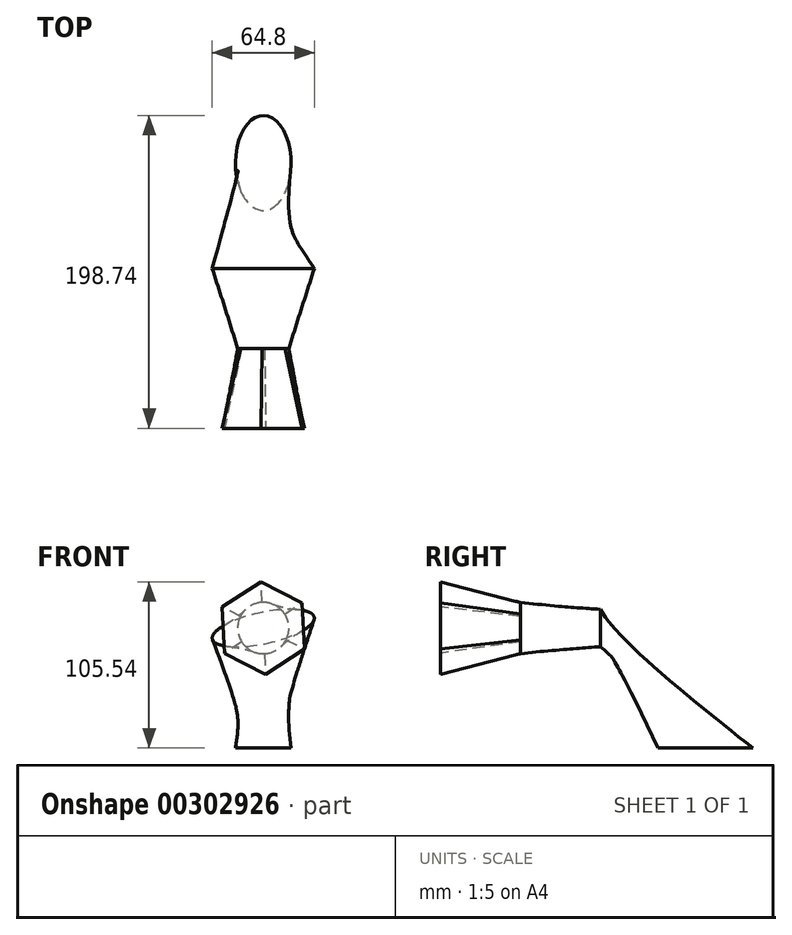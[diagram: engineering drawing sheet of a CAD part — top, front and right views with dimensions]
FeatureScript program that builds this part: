
annotation { "Feature Type Name" : "Feature", "Feature Type Description" : "" }
export const myFeature = defineFeature(function(context is Context, id is Id, definition is map)
    precondition{}
    {
        {
            var Q0;
            Q0=qCreatedBy(makeId("Front.planeOp"),FACE);
            var sketch = newSketch(context, id + "F0", { "sketchPlane" : qUnion([Q0])});
            skEllipse(sketch, "E0", {"center": v(0, 0) * mm, "majorRadius": 33.07 * mm, "minorRadius": 9.9 * mm, "majorAxis": v(0.98, 0.2)});
            skSolve(sketch);
        }
        {
            var Q0;
            Q0=qCreatedBy(makeId("Front.planeOp"),FACE);
            cPlane(context, id + "F1", {"entities" : qUnion([Q0]), "cplaneType" : CPlaneType.OFFSET, "offset" : 101.6 * mm, "width" : 152.4 * mm, "height" : 152.4 * mm});
        }
        {
            var Q0;
            Q0=qCreatedBy(makeId("Front.planeOp"),FACE);
            cPlane(context, id + "F2", {"entities" : qUnion([Q0]), "cplaneType" : CPlaneType.OFFSET, "offset" : 50.8 * mm, "width" : 152.4 * mm, "height" : 152.4 * mm});
        }
        {
            var Q0;
            Q0=qCreatedBy(id+"F2.planeOp",FACE);
            var sketch = newSketch(context, id + "F3", { "sketchPlane" : qUnion([Q0])});
            skCircle(sketch, "E1", {"center": v(0, 0) * mm, "radius": 16.28 * mm});
            skSolve(sketch);
        }
        {
            var Q0;
            Q0=qCreatedBy(id+"F1.planeOp",FACE);
            var sketch = newSketch(context, id + "F4", { "sketchPlane" : qUnion([Q0])});
            skCircle(sketch, "E2.cCircle", {"center": v(0, 0) * mm, "radius": 25.45 * mm, "construction": true});
            skLineSegment(sketch, "E2.0", {"start": v(26.17, -13.37) * mm, "end": v(1.5, -29.34) * mm});
            skLineSegment(sketch, "E2.1", {"start": v(1.5, -29.34) * mm, "end": v(-24.66, -15.98) * mm});
            skLineSegment(sketch, "E2.2", {"start": v(-24.66, -15.98) * mm, "end": v(-26.17, 13.37) * mm});
            skLineSegment(sketch, "E2.3", {"start": v(-26.17, 13.37) * mm, "end": v(-1.5, 29.34) * mm});
            skLineSegment(sketch, "E2.4", {"start": v(-1.5, 29.34) * mm, "end": v(24.66, 15.98) * mm});
            skLineSegment(sketch, "E2.5", {"start": v(24.66, 15.98) * mm, "end": v(26.17, -13.37) * mm});
            skPoint(sketch, "E2.0.midPoint", {"position": v(13.84, -21.36) * mm});
            skSolve(sketch);
        }
        {
            var Q0;
            Q0=makeQuery(id+"F0.imprint","IMPRINT",FACE,{"disambiguationData":[TD([[makeQuery(id+"F0.imprint","IMPRINT",EDGE,{"derivedFrom":sQuery(id+"F0.wireOp",EDGE,"E0")}),1.0]])]});
            var Q1;
            Q1=makeQuery(id+"F3.imprint","IMPRINT",FACE,{"disambiguationData":[TD([[makeQuery(id+"F3.imprint","IMPRINT",EDGE,{"derivedFrom":sQuery(id+"F3.wireOp",EDGE,"E1")}),1.0]])]});
            loft(context, id + "F5", {"sheetProfilesArray" : [{ "sheetProfileEntities" : qUnion([Q0]) }, { "sheetProfileEntities" : qUnion([Q1]) }]});
        }
        {
            var Q1;
            Q1=makeQuery(id+"F5.opLoft","CAP_FACE",FACE,{"disambiguationData":[OSD([makeQuery(id+"F3.imprint","IMPRINT",FACE,{"disambiguationData":[TD([[makeQuery(id+"F3.imprint","IMPRINT",EDGE,{"derivedFrom":sQuery(id+"F3.wireOp",EDGE,"E1")}),1.0]])]})])],"isStart":true});
            var Q2;
            Q2=makeQuery(id+"F4.imprint","IMPRINT",FACE,{"disambiguationData":[TD([[makeQuery(id+"F4.imprint","IMPRINT",EDGE,{"derivedFrom":sQuery(id+"F4.wireOp",EDGE,"E2.0")}),-1.0]])]});
            loft(context, id + "F6", {"operationType" : NewBodyOperationType.ADD, "sheetProfilesArray" : [{ "sheetProfileEntities" : qUnion([Q1]) }, { "sheetProfileEntities" : qUnion([Q2]) }]});
        }
        {
            var Q0;
            Q0=qCreatedBy(makeId("Top.planeOp"),FACE);
            cPlane(context, id + "F7", {"entities" : qUnion([Q0]), "cplaneType" : CPlaneType.OFFSET, "offset" : 76.2 * mm, "oppositeDirection" : true, "width" : 152.4 * mm, "height" : 152.4 * mm});
        }
        {
            var Q0;
            Q0=qCreatedBy(id+"F7.planeOp",FACE);
            var sketch = newSketch(context, id + "F8", { "sketchPlane" : qUnion([Q0])});
            skEllipse(sketch, "E3", {"center": v(0, 66.96) * mm, "majorRadius": 30.18 * mm, "minorRadius": 17.67 * mm, "majorAxis": v(0, -1)});
            skSolve(sketch);
        }
        {
            var Q1;
            Q1=makeQuery(id+"F5.opLoft","CAP_FACE",FACE,{"disambiguationData":[OSD([makeQuery(id+"F0.imprint","IMPRINT",FACE,{"disambiguationData":[TD([[makeQuery(id+"F0.imprint","IMPRINT",EDGE,{"derivedFrom":sQuery(id+"F0.wireOp",EDGE,"E0")}),1.0]])]})])],"isStart":true});
            var Q2;
            Q2=makeQuery(id+"F8.imprint","IMPRINT",FACE,{"disambiguationData":[TD([[makeQuery(id+"F8.imprint","IMPRINT",EDGE,{"derivedFrom":sQuery(id+"F8.wireOp",EDGE,"E3")}),1.0]])]});
            loft(context, id + "F9", {"operationType" : NewBodyOperationType.ADD, "sheetProfilesArray" : [{ "sheetProfileEntities" : qUnion([Q1]) }, { "sheetProfileEntities" : qUnion([Q2]) }]});
        }
    });
